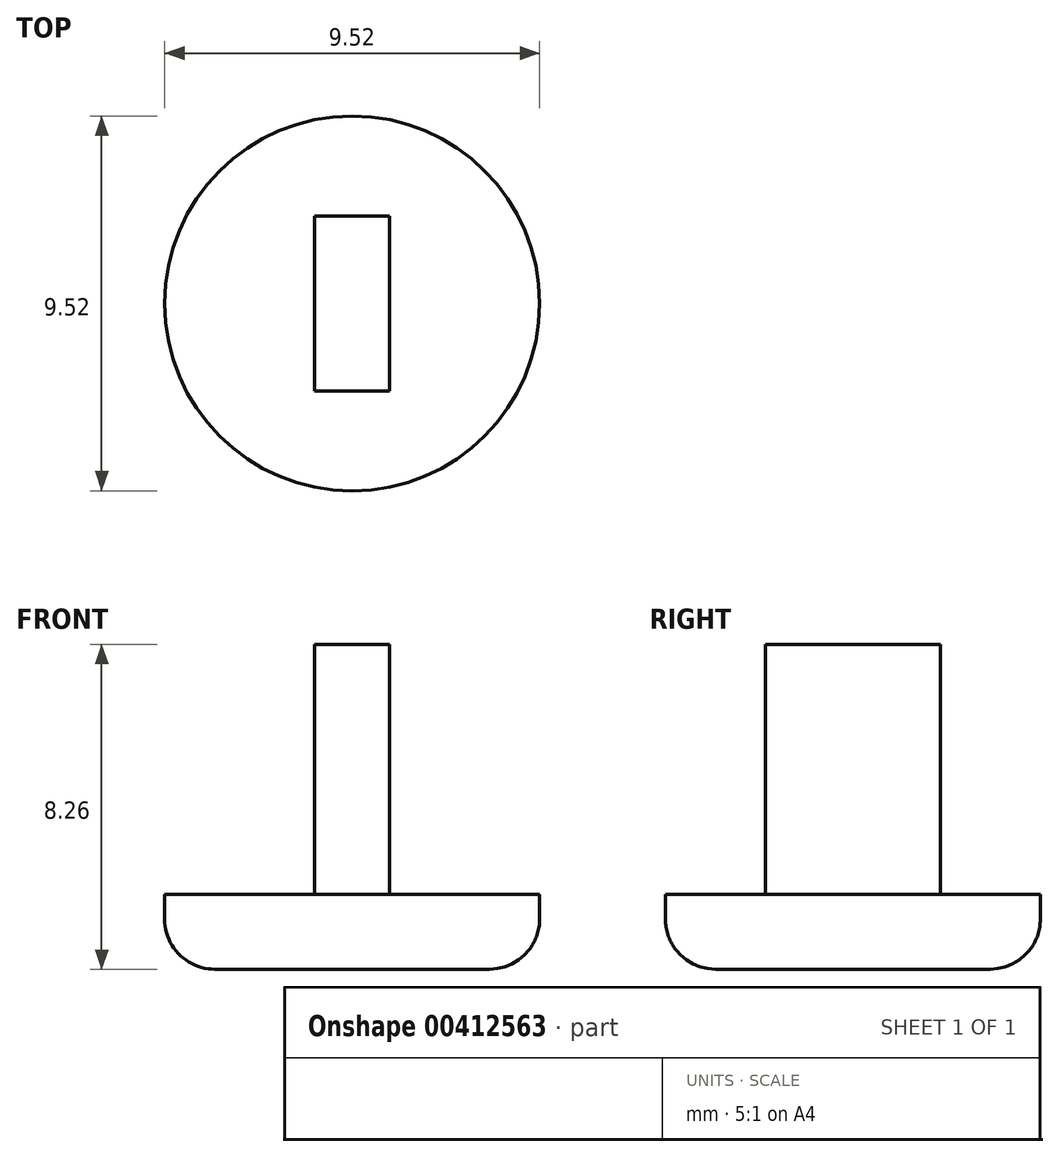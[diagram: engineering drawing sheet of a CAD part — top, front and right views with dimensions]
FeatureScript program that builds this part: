
annotation { "Feature Type Name" : "Feature", "Feature Type Description" : "" }
export const myFeature = defineFeature(function(context is Context, id is Id, definition is map)
    precondition{}
    {
        {
            var Q0;
            Q0=qCreatedBy(makeId("Right.planeOp"),FACE);
            var sketch = newSketch(context, id + "F0", { "sketchPlane" : qUnion([Q0])});
            skLineSegment(sketch, "E0", {"start": v(0, 0) * mm, "end": v(-4.76, 0) * mm});
            skLineSegment(sketch, "E1", {"start": v(0, 0) * mm, "end": v(0, -1.9) * mm});
            skLineSegment(sketch, "E2.bottom", {"start": v(0, -1.9) * mm, "end": v(-4.76, -1.9) * mm});
            skLineSegment(sketch, "E2.left", {"start": v(0, -1.9) * mm, "end": v(0, 0) * mm});
            skLineSegment(sketch, "E2.right", {"start": v(-4.76, -1.9) * mm, "end": v(-4.76, 0) * mm});
            skSolve(sketch);
        }
        {
            var Q0;
            Q0=makeQuery(id+"F0.imprint","IMPRINT",FACE,{"disambiguationData":[TD([[makeQuery(id+"F0.imprint","IMPRINT",EDGE,{"derivedFrom":sQuery(id+"F0.wireOp",EDGE,"E2.bottom")}),-1.0]])]});
            var Q1;
            Q1=sQuery(id+"F0.wireOp",EDGE,"E2.left");
            revolve(context, id + "F1", {"entities" : qUnion([Q0]), "axis" : qUnion([Q1]), "revolveType" : RevolveType.FULL});
        }
        {
            var Q0;
            Q0=makeQuery(id+"F1.opRevolve","SWEPT_FACE",FACE,{"disambiguationData":[OSD([sQuery(id+"F0.wireOp",EDGE,"E0")])]});
            var sketch = newSketch(context, id + "F2", { "sketchPlane" : qUnion([Q0])});
            skLineSegment(sketch, "E3.bottom", {"start": v(-0.95, 2.22) * mm, "end": v(0.95, 2.22) * mm});
            skLineSegment(sketch, "E3.top", {"start": v(-0.95, -2.22) * mm, "end": v(0.95, -2.22) * mm});
            skLineSegment(sketch, "E3.left", {"start": v(-0.95, 2.22) * mm, "end": v(-0.95, -2.22) * mm});
            skLineSegment(sketch, "E3.right", {"start": v(0.95, 2.22) * mm, "end": v(0.95, -2.22) * mm});
            skPoint(sketch, "E3.middle", {"position": v(0, 0) * mm});
            skSolve(sketch);
        }
        {
            var Q0;
            Q0=makeQuery(id+"F2.imprint","IMPRINT",FACE,{"disambiguationData":[TD([[makeQuery(id+"F2.imprint","IMPRINT",EDGE,{"derivedFrom":sQuery(id+"F2.wireOp",EDGE,"E3.bottom")}),-1.0]])]});
            extrude(context, id + "F3", {"entities" : qUnion([Q0]), "depth" : 6.35 * mm});
        }
        {
            var Q0;
            Q0=makeQuery(id+"F1.opRevolve","SWEPT_EDGE",EDGE,{"disambiguationData":[OSD([sQuery(id+"F0.wireOp",EDGE,"E2.bottom"),sQuery(id+"F0.wireOp",EDGE,"E2.right")])]});
            fillet(context, id + "F4", {"entities" : qUnion([Q0]), "radius" : 1.27 * mm, "tangentPropagation" : true, "allowEdgeOverflow" : false});
        }
    });
